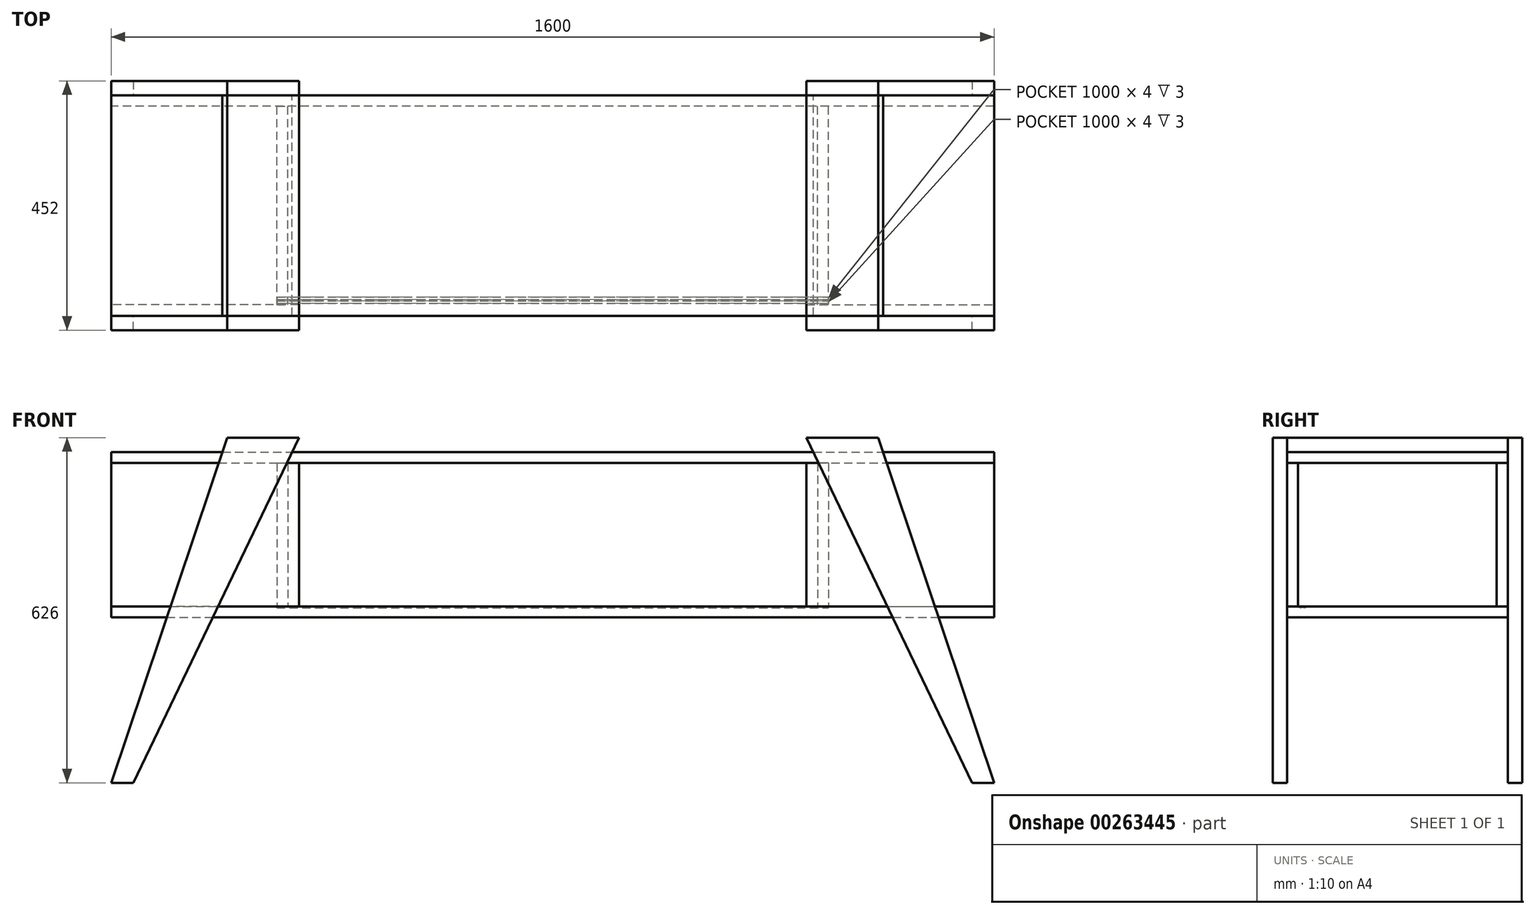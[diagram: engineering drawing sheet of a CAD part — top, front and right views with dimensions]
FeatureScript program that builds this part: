
annotation { "Feature Type Name" : "Feature", "Feature Type Description" : "" }
export const myFeature = defineFeature(function(context is Context, id is Id, definition is map)
    precondition{}
    {
        {
            assignVariable(context, id + "F0", {"name" : "Long", "anyValue" : 1600});
        }
        {
            assignVariable(context, id + "F1", {"name" : "Prof", "anyValue" : 400});
        }
        {
            assignVariable(context, id + "F2", {"name" : "EpP", "anyValue" : 20});
        }
        {
            assignVariable(context, id + "F3", {"name" : "EpFoot", "anyValue" : 26});
        }
        {
            assignVariable(context, id + "F4", {"name" : "EpPortes", "anyValue" : 3});
        }
        {
            var Q0;
            Q0=qCreatedBy(makeId("Front.planeOp"),FACE);
            var sketch = newSketch(context, id + "F5", { "sketchPlane" : qUnion([Q0])});
            skLineSegment(sketch, "E0.bottom", {"start": v(-800, 580) * mm, "end": v(800, 580) * mm});
            skLineSegment(sketch, "E0.top", {"start": v(-800, 600) * mm, "end": v(800, 600) * mm});
            skLineSegment(sketch, "E0.left", {"start": v(-800, 580) * mm, "end": v(-800, 600) * mm});
            skLineSegment(sketch, "E0.right", {"start": v(800, 580) * mm, "end": v(800, 600) * mm});
            skLineSegment(sketch, "E1", {"start": v(-1523.7, 450) * mm, "end": v(1632.53, 450) * mm, "construction": true});
            skLineSegment(sketch, "E2.MirrorCS", {"start": v(-800, 320) * mm, "end": v(-800, 300) * mm});
            skLineSegment(sketch, "E3.MirrorCS", {"start": v(800, 320) * mm, "end": v(800, 300) * mm});
            skLineSegment(sketch, "E4.MirrorCS", {"start": v(-800, 300) * mm, "end": v(800, 300) * mm});
            skLineSegment(sketch, "E5.MirrorCS", {"start": v(-800, 320) * mm, "end": v(800, 320) * mm});
            skSolve(sketch);
        }
        {
            var Q0;
            Q0 = qSketchRegion(id + "F5", true);
            extrude(context, id + "F6", {"entities" : qUnion([Q0]), "endBound" : BoundingType.SYMMETRIC, "depth" : (getVariable(context, 'Prof')) * mm});
        }
        {
            var Q0;
            Q0=qCreatedBy(makeId("Right.planeOp"),FACE);
            var sketch = newSketch(context, id + "F7", { "sketchPlane" : qUnion([Q0])});
            skLineSegment(sketch, "E6.bottom", {"start": v(200, 580) * mm, "end": v(180, 580) * mm});
            skLineSegment(sketch, "E6.top", {"start": v(200, 320) * mm, "end": v(180, 320) * mm});
            skLineSegment(sketch, "E6.left", {"start": v(200, 580) * mm, "end": v(200, 320) * mm});
            skLineSegment(sketch, "E6.right", {"start": v(180, 580) * mm, "end": v(180, 320) * mm});
            skSolve(sketch);
        }
        {
            var Q0;
            Q0 = qSketchRegion(id + "F7", true);
            extrude(context, id + "F8", {"entities" : qUnion([Q0]), "endBound" : BoundingType.SYMMETRIC, "depth" : getVariable(context, 'Long') * mm});
        }
        {
            var Q0;
            Q0=qCreatedBy(makeId("Front.planeOp"),FACE);
            var sketch = newSketch(context, id + "F9", { "sketchPlane" : qUnion([Q0])});
            skLineSegment(sketch, "E7.bottom", {"start": v(-500, 580) * mm, "end": v(-480, 580) * mm});
            skLineSegment(sketch, "E7.top", {"start": v(-500, 320) * mm, "end": v(-480, 320) * mm});
            skLineSegment(sketch, "E7.left", {"start": v(-500, 580) * mm, "end": v(-500, 320) * mm});
            skLineSegment(sketch, "E7.right", {"start": v(-480, 580) * mm, "end": v(-480, 320) * mm});
            skSolve(sketch);
        }
        {
            var Q0;
            Q0 = qSketchRegion(id + "F9", true);
            extrude(context, id + "F10", {"entities" : qUnion([Q0]), "endBound" : BoundingType.SYMMETRIC, "depth" : (getVariable(context, 'Prof') - 2 * getVariable(context, 'EpP')) * mm});
        }
        {
            var Q0;
            Q0=makeQuery(id+"F10.opExtrude","SWEPT_BODY",BODY,{"disambiguationData":[OSD([sQuery(id+"F9.wireOp",EDGE,"E7.bottom"),sQuery(id+"F9.wireOp",EDGE,"E7.top"),sQuery(id+"F9.wireOp",EDGE,"E7.left"),sQuery(id+"F9.wireOp",EDGE,"E7.right")])]});
            var Q1;
            Q1=qCreatedBy(makeId("Right.planeOp"),FACE);
            mirror(context, id + "F11", {"entities" : qUnion([Q0]), "mirrorPlane" : qUnion([Q1])});
        }
        {
            var Q0;
            Q0=makeQuery(id+"F10.opExtrude","SWEPT_FACE",FACE,{"disambiguationData":[OSD([sQuery(id+"F9.wireOp",EDGE,"E7.right")])]});
            var sketch = newSketch(context, id + "F12", { "sketchPlane" : qUnion([Q0])});
            skLineSegment(sketch, "E8.bottom", {"start": v(-200, 580) * mm, "end": v(-180, 580) * mm});
            skLineSegment(sketch, "E8.top", {"start": v(-200, 320) * mm, "end": v(-180, 320) * mm});
            skLineSegment(sketch, "E8.left", {"start": v(-200, 580) * mm, "end": v(-200, 320) * mm});
            skLineSegment(sketch, "E8.right", {"start": v(-180, 580) * mm, "end": v(-180, 320) * mm});
            skSolve(sketch);
        }
        {
            var Q0;
            Q0 = qSketchRegion(id + "F12", true);
            var Q1;
            Q1=makeQuery(id+"F6.opExtrude","SWEPT_FACE",FACE,{"disambiguationData":[OSD([sQuery(id+"F5.wireOp",EDGE,"E0.left")])]});
            extrude(context, id + "F13", {"entities" : qUnion([Q0]), "depth" : (getVariable(context, 'EpP')) * mm, "hasSecondDirection" : true, "secondDirectionBound" : SecondDirectionBoundingType.UP_TO_SURFACE, "secondDirectionOppositeDirection" : true, "secondDirectionBoundEntityFace" : qUnion([Q1]), "secondDirectionDepth" : 25 * mm});
        }
        {
            var Q0;
            Q0=makeQuery(id+"F13.opExtrude","SWEPT_BODY",BODY,{"disambiguationData":[OSD([sQuery(id+"F12.wireOp",EDGE,"E8.bottom"),sQuery(id+"F12.wireOp",EDGE,"E8.top"),sQuery(id+"F12.wireOp",EDGE,"E8.left"),sQuery(id+"F12.wireOp",EDGE,"E8.right")])]});
            var Q1;
            Q1=qCreatedBy(makeId("Right.planeOp"),FACE);
            mirror(context, id + "F14", {"entities" : qUnion([Q0]), "mirrorPlane" : qUnion([Q1])});
        }
        {
            var Q0;
            Q0=makeQuery(id+"F6.opExtrude","SWEPT_FACE",FACE,{"disambiguationData":[OSD([sQuery(id+"F5.wireOp",EDGE,"E5.MirrorCS")])]});
            var sketch = newSketch(context, id + "F15", { "sketchPlane" : qUnion([Q0])});
            skLineSegment(sketch, "E9.bottom", {"start": v(-500, -173) * mm, "end": v(500, -173) * mm});
            skLineSegment(sketch, "E9.top", {"start": v(-500, -177) * mm, "end": v(500, -177) * mm});
            skLineSegment(sketch, "E9.left", {"start": v(-500, -173) * mm, "end": v(-500, -177) * mm});
            skLineSegment(sketch, "E9.right", {"start": v(500, -173) * mm, "end": v(500, -177) * mm});
            skLineSegment(sketch, "E10.bottom", {"start": v(-500, -166) * mm, "end": v(500, -166) * mm});
            skLineSegment(sketch, "E10.top", {"start": v(-500, -170) * mm, "end": v(500, -170) * mm});
            skLineSegment(sketch, "E10.left", {"start": v(-500, -166) * mm, "end": v(-500, -170) * mm});
            skLineSegment(sketch, "E10.right", {"start": v(500, -166) * mm, "end": v(500, -170) * mm});
            skSolve(sketch);
        }
        {
            var Q0;
            Q0 = qSketchRegion(id + "F15", true);
            extrude(context, id + "F16", {"entities" : qUnion([Q0]), "operationType" : NewBodyOperationType.REMOVE, "oppositeDirection" : true, "depth" : (getVariable(context, 'EpPortes')) * mm});
        }
        {
            var Q0;
            Q0=makeQuery(id+"F6.opExtrude","CAP_FACE",FACE,{"disambiguationData":[OSD([sQuery(id+"F5.wireOp",EDGE,"E2.MirrorCS"),sQuery(id+"F5.wireOp",EDGE,"E3.MirrorCS"),sQuery(id+"F5.wireOp",EDGE,"E4.MirrorCS"),sQuery(id+"F5.wireOp",EDGE,"E5.MirrorCS")])],"isStart":false});
            var sketch = newSketch(context, id + "F17", { "sketchPlane" : qUnion([Q0])});
            skLineSegment(sketch, "E11", {"start": v(-800, 0) * mm, "end": v(-590, 626) * mm});
            skLineSegment(sketch, "E12", {"start": v(-590, 626) * mm, "end": v(-460, 626) * mm});
            skLineSegment(sketch, "E13", {"start": v(-460, 626) * mm, "end": v(-760, 0) * mm});
            skLineSegment(sketch, "E14", {"start": v(-760, 0) * mm, "end": v(-800, 0) * mm});
            skSolve(sketch);
        }
        {
            var Q0;
            Q0 = qSketchRegion(id + "F17", true);
            extrude(context, id + "F18", {"entities" : qUnion([Q0]), "depth" : (getVariable(context, 'EpFoot')) * mm});
        }
        {
            var Q0;
            Q0=makeQuery(id+"F18.opExtrude","SWEPT_BODY",BODY,{"disambiguationData":[OSD([sQuery(id+"F17.wireOp",EDGE,"E11"),sQuery(id+"F17.wireOp",EDGE,"E12"),sQuery(id+"F17.wireOp",EDGE,"E13"),sQuery(id+"F17.wireOp",EDGE,"E14")])]});
            var Q1;
            Q1=qCreatedBy(makeId("Right.planeOp"),FACE);
            mirror(context, id + "F19", {"entities" : qUnion([Q0]), "mirrorPlane" : qUnion([Q1])});
        }
        {
            var Q0;
            Q0=makeQuery(id+"F18.opExtrude","SWEPT_BODY",BODY,{"disambiguationData":[OSD([sQuery(id+"F17.wireOp",EDGE,"E11"),sQuery(id+"F17.wireOp",EDGE,"E12"),sQuery(id+"F17.wireOp",EDGE,"E13"),sQuery(id+"F17.wireOp",EDGE,"E14")])]});
            var Q1;
            Q1=qCreatedBy(makeId("Front.planeOp"),FACE);
            mirror(context, id + "F20", {"entities" : qUnion([Q0]), "mirrorPlane" : qUnion([Q1])});
        }
        {
            var Q0;
            Q0=makeQuery(id+"F19.opPattern","COPY",BODY,{"derivedFrom":makeQuery(id+"F18.opExtrude","SWEPT_BODY",BODY,{"disambiguationData":[OSD([sQuery(id+"F17.wireOp",EDGE,"E11"),sQuery(id+"F17.wireOp",EDGE,"E12"),sQuery(id+"F17.wireOp",EDGE,"E13"),sQuery(id+"F17.wireOp",EDGE,"E14")])]}),"instanceName":"1"});
            var Q1;
            Q1=qCreatedBy(makeId("Front.planeOp"),FACE);
            mirror(context, id + "F21", {"entities" : qUnion([Q0]), "mirrorPlane" : qUnion([Q1])});
        }
        {
            var Q0;
            Q0=makeQuery(id+"F20.opPattern","COPY",FACE,{"derivedFrom":makeQuery(id+"F18.opExtrude","CAP_FACE",FACE,{"disambiguationData":[OSD([sQuery(id+"F17.wireOp",EDGE,"E11"),sQuery(id+"F17.wireOp",EDGE,"E12"),sQuery(id+"F17.wireOp",EDGE,"E13"),sQuery(id+"F17.wireOp",EDGE,"E14")])],"isStart":true}),"instanceName":"1"});
            var sketch = newSketch(context, id + "F22", { "sketchPlane" : qUnion([Q0])});
            skLineSegment(sketch, "E15", {"start": v(-598.72, 600) * mm, "end": v(-590, 626) * mm});
            skLineSegment(sketch, "E16", {"start": v(-590, 626) * mm, "end": v(-460, 626) * mm});
            skLineSegment(sketch, "E17", {"start": v(-460, 626) * mm, "end": v(-472.46, 600) * mm});
            skLineSegment(sketch, "E18", {"start": v(-472.46, 600) * mm, "end": v(-598.72, 600) * mm});
            skSolve(sketch);
        }
        {
            var Q0;
            Q0 = qSketchRegion(id + "F22", true);
            var Q1;
            Q1=makeQuery(id+"F18.opExtrude","CAP_FACE",FACE,{"disambiguationData":[OSD([sQuery(id+"F17.wireOp",EDGE,"E11"),sQuery(id+"F17.wireOp",EDGE,"E12"),sQuery(id+"F17.wireOp",EDGE,"E13"),sQuery(id+"F17.wireOp",EDGE,"E14")])],"isStart":true});
            extrude(context, id + "F23", {"entities" : qUnion([Q0]), "endBound" : BoundingType.UP_TO_SURFACE, "endBoundEntityFace" : qUnion([Q1]), "depth" : 25 * mm});
        }
        {
            var Q0;
            Q0=makeQuery(id+"F23.opExtrude","SWEPT_BODY",BODY,{"disambiguationData":[OSD([sQuery(id+"F22.wireOp",EDGE,"E15"),sQuery(id+"F22.wireOp",EDGE,"E16"),sQuery(id+"F22.wireOp",EDGE,"E17"),sQuery(id+"F22.wireOp",EDGE,"E18")])]});
            var Q1;
            Q1=qCreatedBy(makeId("Right.planeOp"),FACE);
            mirror(context, id + "F24", {"entities" : qUnion([Q0]), "mirrorPlane" : qUnion([Q1])});
        }
    });
